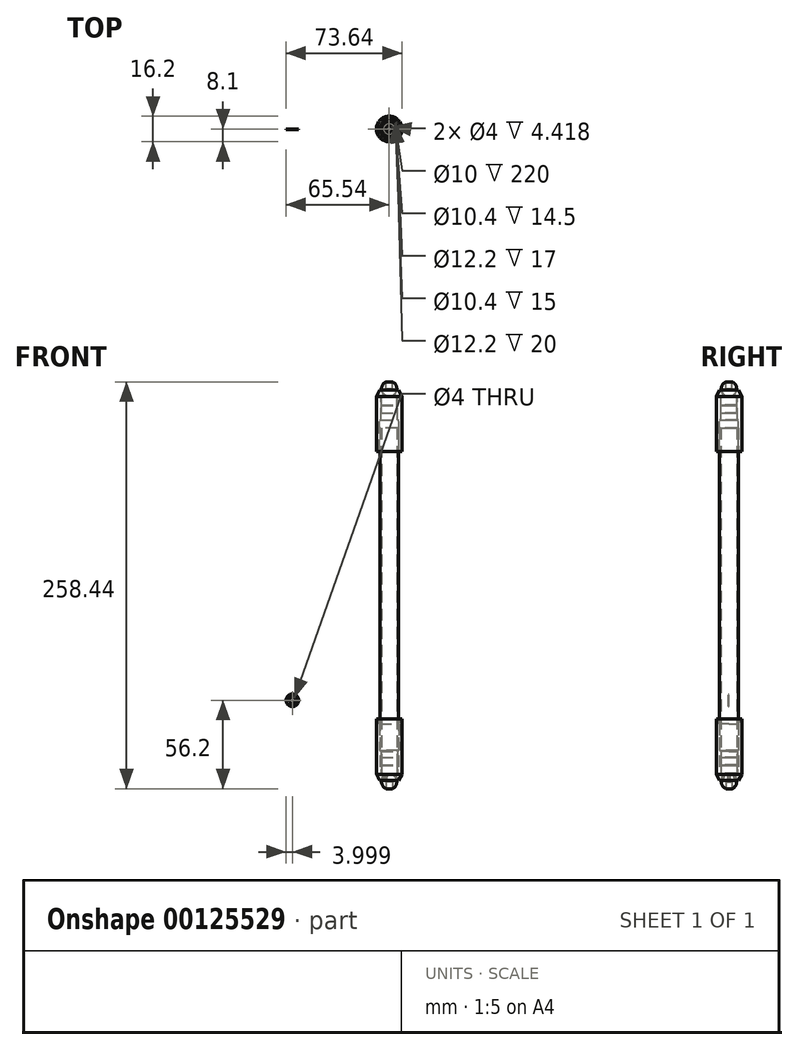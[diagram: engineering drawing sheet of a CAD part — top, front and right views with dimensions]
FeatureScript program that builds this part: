
annotation { "Feature Type Name" : "Feature", "Feature Type Description" : "" }
export const myFeature = defineFeature(function(context is Context, id is Id, definition is map)
    precondition{}
    {
        {
            var Q0;
            Q0=qCreatedBy(makeId("Front.planeOp"),FACE);
            var sketch = newSketch(context, id + "F0", { "sketchPlane" : qUnion([Q0])});
            skLineSegment(sketch, "E0", {"start": v(-5.03, 0.7) * mm, "end": v(-6.03, 0.7) * mm});
            skLineSegment(sketch, "E1", {"start": v(-8.1, 4.8) * mm, "end": v(-8.1, 39.8) * mm});
            skLineSegment(sketch, "E2", {"start": v(-8.1, 39.8) * mm, "end": v(-6.1, 39.8) * mm});
            skLineSegment(sketch, "E3", {"start": v(-6.1, 39.8) * mm, "end": v(-6.1, 19.8) * mm});
            skLineSegment(sketch, "E4", {"start": v(-6.1, 19.8) * mm, "end": v(-5.2, 19.8) * mm});
            skLineSegment(sketch, "E5", {"start": v(-5.2, 19.8) * mm, "end": v(-5.2, 4.8) * mm});
            skLineSegment(sketch, "E6", {"start": v(-5.2, 4.8) * mm, "end": v(-3.11, 4.8) * mm});
            skLineSegment(sketch, "E7", {"start": v(0, 5.2) * mm, "end": v(0, 4.8) * mm});
            skLineSegment(sketch, "E8", {"start": v(-6.03, 0.7) * mm, "end": v(-8.1, 4.8) * mm});
            skLineSegment(sketch, "E9", {"start": v(0, 0) * mm, "end": v(0, 32.36) * mm, "construction": true});
            skLineSegment(sketch, "E10", {"start": v(2.85, 3.2) * mm, "end": v(-9.79, 3.2) * mm, "construction": true});
            skCircle(sketch, "E11", {"center": v(0, 0) * mm, "radius": 4.85 * mm});
            skLineSegment(sketch, "E12", {"start": v(0, 4.8) * mm, "end": v(0, -4.85) * mm});
            skLineSegment(sketch, "E13", {"start": v(0, 15.55) * mm, "end": v(-5, 15.55) * mm});
            skLineSegment(sketch, "E14", {"start": v(-5, 15.55) * mm, "end": v(-5, 10.55) * mm});
            skLineSegment(sketch, "E15", {"start": v(-5, 10.55) * mm, "end": v(0, 10.55) * mm});
            skLineSegment(sketch, "E16", {"start": v(0, 10.55) * mm, "end": v(0, 15.55) * mm});
            skLineSegment(sketch, "E17", {"start": v(0, 5.3) * mm, "end": v(-5, 5.3) * mm});
            skLineSegment(sketch, "E18", {"start": v(-5, 5.3) * mm, "end": v(-5, 10.3) * mm});
            skLineSegment(sketch, "E19", {"start": v(-5, 10.3) * mm, "end": v(0, 10.3) * mm});
            skLineSegment(sketch, "E20", {"start": v(0, 10.3) * mm, "end": v(0, 5.3) * mm});
            skLineSegment(sketch, "E21", {"start": v(-4, 2.74) * mm, "end": v(4, 2.74) * mm, "construction": true});
            skLineSegment(sketch, "E22", {"start": v(0, 11.48) * mm, "end": v(-8.67, -7.13) * mm, "construction": true});
            skLineSegment(sketch, "E23", {"start": v(-5.03, 0.7) * mm, "end": v(-3.11, 4.8) * mm});
            skPoint(sketch, "E24", {"position": v(-4.4, 2.05) * mm});
            skSolve(sketch);
        }
        {
            var Q0;
            Q0=makeQuery(id+"F0.imprint","IMPRINT",FACE,{"disambiguationData":[TD([[makeQuery(id+"F0.imprint","IMPRINT",EDGE,{"derivedFrom":sQuery(id+"F0.wireOp",EDGE,"E13")}),1.0]])]});
            var Q1;
            Q1=makeQuery(id+"F0.imprint","IMPRINT",FACE,{"disambiguationData":[TD([[makeQuery(id+"F0.imprint","IMPRINT",EDGE,{"derivedFrom":sQuery(id+"F0.wireOp",EDGE,"E17")}),-1.0]])]});
            var Q2;
            {var subQ0=sQuery(id+"F0.wireOp",EDGE,"E12");Q2=makeQuery(id+"F0.imprint","IMPRINT",FACE,{"disambiguationData":[TD([[makeQuery(id+"F0.imprint","IMPRINT",EDGE,{"derivedFrom":subQ0}),-1.0]])]});}
            var Q3;
            {var subQ0=sQuery(id+"F0.wireOp",EDGE,"E0");Q3=makeQuery(id+"F0.imprint","IMPRINT",FACE,{"disambiguationData":[TD([[makeQuery(id+"F0.imprint","IMPRINT",EDGE,{"derivedFrom":subQ0}),-1.0]])]});}
            var Q4;
            Q4=sQuery(id+"F0.wireOp",EDGE,"E9");
            revolve(context, id + "F1", {"entities" : qUnion([Q0, Q1, Q2, Q3]), "axis" : qUnion([Q4]), "revolveType" : RevolveType.FULL});
        }
        {
            var Q0;
            Q0=makeQuery(id+"F1.opRevolve","SWEPT_FACE",FACE,{"disambiguationData":[OSD([sQuery(id+"F0.wireOp",EDGE,"E6")])]});
            var sketch = newSketch(context, id + "F2", { "sketchPlane" : qUnion([Q0])});
            skCircle(sketch, "E25", {"center": v(0, 0) * mm, "radius": 6 * mm});
            skCircle(sketch, "E26", {"center": v(0, 0) * mm, "radius": 5 * mm});
            skSolve(sketch);
        }
        {
            var Q0;
            Q0=makeQuery(id+"F2.imprint","IMPRINT",FACE,{"disambiguationData":[TD([[makeQuery(id+"F2.imprint","IMPRINT",EDGE,{"derivedFrom":sQuery(id+"F2.wireOp",EDGE,"E26")}),-1.0]])]});
            var Q1;
            Q1=makeQuery(id+"F2.imprint","IMPRINT",FACE,{"disambiguationData":[TD([[makeQuery(id+"F2.imprint","IMPRINT",EDGE,{"derivedFrom":sQuery(id+"F2.wireOp",EDGE,"E25")}),1.0]])]});
            extrude(context, id + "F3", {"entities" : qUnion([Q0, Q1]), "depth" : 220 * mm});
        }
        {
            var Q0;
            Q0=makeQuery(id+"F3.opExtrude","CAP_FACE",FACE,{"disambiguationData":[OSD([sQuery(id+"F0.wireOp",EDGE,"E4"),sQuery(id+"F0.wireOp",EDGE,"E5"),sQuery(id+"F2.wireOp",EDGE,"E26")])],"isStart":false});
            cPlane(context, id + "F4", {"entities" : qUnion([Q0]), "cplaneType" : CPlaneType.OFFSET, "offset" : 100 * mm, "oppositeDirection" : true, "width" : 150 * mm, "height" : 150 * mm});
        }
        {
            var Q0;
            Q0=qCreatedBy(makeId("Top.planeOp"),FACE);
            cPlane(context, id + "F5", {"entities" : qUnion([Q0]), "cplaneType" : CPlaneType.OFFSET, "offset" : 5 * mm, "oppositeDirection" : true, "width" : 150 * mm, "height" : 150 * mm});
        }
        {
            var Q0;
            Q0=qCreatedBy(id+"F5.planeOp",FACE);
            var sketch = newSketch(context, id + "F6", { "sketchPlane" : qUnion([Q0])});
            skCircle(sketch, "E27", {"center": v(0, 0) * mm, "radius": 2 * mm});
            skSolve(sketch);
        }
        {
            var Q0;
            Q0=makeQuery(id+"F6.imprint","IMPRINT",FACE,{"disambiguationData":[TD([[makeQuery(id+"F6.imprint","IMPRINT",EDGE,{"derivedFrom":sQuery(id+"F6.wireOp",EDGE,"E27")}),1.0]])]});
            extrude(context, id + "F7", {"entities" : qUnion([Q0]), "operationType" : NewBodyOperationType.REMOVE, "depth" : 5 * mm});
        }
        {
            var Q0;
            Q0=makeQuery(id+"F1.opRevolve","SWEPT_BODY",BODY,{"disambiguationData":[OSD([sQuery(id+"F0.wireOp",EDGE,"E17"),sQuery(id+"F0.wireOp",EDGE,"E18"),sQuery(id+"F0.wireOp",EDGE,"E19"),sQuery(id+"F0.wireOp",EDGE,"E20")])]});
            var Q1;
            Q1=makeQuery(id+"F1.opRevolve","SWEPT_BODY",BODY,{"disambiguationData":[OSD([sQuery(id+"F0.wireOp",EDGE,"E13"),sQuery(id+"F0.wireOp",EDGE,"E14"),sQuery(id+"F0.wireOp",EDGE,"E15"),sQuery(id+"F0.wireOp",EDGE,"E16")])]});
            var Q2;
            Q2=makeQuery(id+"F1.opRevolve","SWEPT_BODY",BODY,{"disambiguationData":[OSD([sQuery(id+"F0.wireOp",EDGE,"E11"),sQuery(id+"F0.wireOp",EDGE,"E12")])]});
            var Q3;
            Q3=makeQuery(id+"F1.opRevolve","SWEPT_BODY",BODY,{"disambiguationData":[OSD([sQuery(id+"F0.wireOp",EDGE,"841e1b56-2235-48bc-aee3-342361c37d41"),sQuery(id+"F0.wireOp",EDGE,"E0"),sQuery(id+"F0.wireOp",EDGE,"E1"),sQuery(id+"F0.wireOp",EDGE,"E2"),sQuery(id+"F0.wireOp",EDGE,"E3"),sQuery(id+"F0.wireOp",EDGE,"E4"),sQuery(id+"F0.wireOp",EDGE,"E5"),sQuery(id+"F0.wireOp",EDGE,"E6"),sQuery(id+"F0.wireOp",EDGE,"E8"),sQuery(id+"F0.wireOp",EDGE,"4b548780-3497-4359-ae85-f4aefd225b06")])]});
            var Q4;
            Q4=qCreatedBy(id+"F4.planeOp",FACE);
            mirror(context, id + "F8", {"entities" : qUnion([Q0, Q1, Q2, Q3]), "mirrorPlane" : qUnion([Q4])});
        }
        {
            var Q0;
            Q0=makeQuery(id+"F1.opRevolve","SWEPT_EDGE",EDGE,{"disambiguationData":[OSD([sQuery(id+"F0.wireOp",EDGE,"E2"),sQuery(id+"F0.wireOp",EDGE,"E3")])]});
            var Q1;
            Q1=makeQuery(id+"F1.opRevolve","SWEPT_EDGE",EDGE,{"disambiguationData":[OSD([sQuery(id+"F0.wireOp",EDGE,"E2"),sQuery(id+"F0.wireOp",EDGE,"E3")])]});
            chamfer(context, id + "F9", {"entities" : qUnion([Q0, Q1]), "chamferType" : ChamferType.TWO_OFFSETS, "width1" : 1 * mm, "oppositeDirection" : false, "width2" : 3 * mm, "tangentPropagation" : true});
        }
        {
            var Q0;
            Q0=qCreatedBy(makeId("Front.planeOp"),FACE);
            var sketch = newSketch(context, id + "F10", { "sketchPlane" : qUnion([Q0])});
            skLineSegment(sketch, "E28", {"start": v(-5.5, 0.7) * mm, "end": v(-3.6, 4.8) * mm});
            skLineSegment(sketch, "E29", {"start": v(-5.5, 0.7) * mm, "end": v(-4.14, 0.7) * mm});
            skLineSegment(sketch, "E30", {"start": v(-4.14, 0.7) * mm, "end": v(-2.47, 4.8) * mm});
            skLineSegment(sketch, "E31", {"start": v(-2.47, 4.8) * mm, "end": v(-3.6, 4.8) * mm});
            skLineSegment(sketch, "E32", {"start": v(0, 0) * mm, "end": v(0, -5.1) * mm, "construction": true});
            skSolve(sketch);
        }
        {
            var Q0;
            Q0=makeQuery(id+"F10.imprint","IMPRINT",FACE,{"disambiguationData":[TD([[makeQuery(id+"F10.imprint","IMPRINT",EDGE,{"derivedFrom":sQuery(id+"F10.wireOp",EDGE,"E28")}),-1.0]])]});
            var Q1;
            Q1=sQuery(id+"F10.wireOp",EDGE,"E32");
            revolve(context, id + "F11", {"entities" : qUnion([Q0]), "axis" : qUnion([Q1]), "revolveType" : RevolveType.SYMMETRIC, "angle" : 108 * degree});
        }
        {
            var Q0;
            Q0=makeQuery(id+"F11.opRevolve","SWEPT_BODY",BODY,{"disambiguationData":[OSD([sQuery(id+"F10.wireOp",EDGE,"E28"),sQuery(id+"F10.wireOp",EDGE,"E29"),sQuery(id+"F10.wireOp",EDGE,"E30"),sQuery(id+"F10.wireOp",EDGE,"E31")])]});
            var Q1;
            Q1=sQuery(id+"F10.wireOp",EDGE,"E32");
            circularPattern(context, id + "F12", {"entities" : qUnion([Q0]), "axis" : qUnion([Q1]), "angle" : 120 * degree, "instanceCount" : 3});
        }
        {
            var Q0;
            Q0=makeQuery(id+"F11.opRevolve","SWEPT_BODY",BODY,{"disambiguationData":[OSD([sQuery(id+"F10.wireOp",EDGE,"E28"),sQuery(id+"F10.wireOp",EDGE,"E29"),sQuery(id+"F10.wireOp",EDGE,"E30"),sQuery(id+"F10.wireOp",EDGE,"E31")])]});
            var Q1;
            Q1=makeQuery(id+"F12.opPattern","COPY",BODY,{"derivedFrom":makeQuery(id+"F11.opRevolve","SWEPT_BODY",BODY,{"disambiguationData":[OSD([sQuery(id+"F10.wireOp",EDGE,"E28"),sQuery(id+"F10.wireOp",EDGE,"E29"),sQuery(id+"F10.wireOp",EDGE,"E30"),sQuery(id+"F10.wireOp",EDGE,"E31")])]}),"instanceName":"2"});
            var Q2;
            Q2=makeQuery(id+"F12.opPattern","COPY",BODY,{"derivedFrom":makeQuery(id+"F11.opRevolve","SWEPT_BODY",BODY,{"disambiguationData":[OSD([sQuery(id+"F10.wireOp",EDGE,"E28"),sQuery(id+"F10.wireOp",EDGE,"E29"),sQuery(id+"F10.wireOp",EDGE,"E30"),sQuery(id+"F10.wireOp",EDGE,"E31")])]}),"instanceName":"1"});
            var Q3;
            Q3=makeQuery(id+"F1.opRevolve","SWEPT_BODY",BODY,{"disambiguationData":[OSD([sQuery(id+"F0.wireOp",EDGE,"E0"),sQuery(id+"F0.wireOp",EDGE,"E1"),sQuery(id+"F0.wireOp",EDGE,"E2"),sQuery(id+"F0.wireOp",EDGE,"E3"),sQuery(id+"F0.wireOp",EDGE,"E5"),sQuery(id+"F0.wireOp",EDGE,"E6"),sQuery(id+"F0.wireOp",EDGE,"E8"),sQuery(id+"F0.wireOp",EDGE,"E23")])]});
            booleanBodies(context, id + "F13", {"operationType" : BooleanOperationType.SUBTRACTION, "tools" : qUnion([Q0, Q1, Q2]), "targets" : qUnion([Q3])});
        }
        {
            var Q0;
            Q0=makeQuery(id+"F13.opBoolean","COPY",EDGE,{"derivedFrom":makeQuery(id+"F11.opRevolve","CAP_EDGE",EDGE,{"disambiguationData":[OSD([sQuery(id+"F10.wireOp",EDGE,"E28")])],"isStart":true})});
            var Q1;
            Q1=makeQuery(id+"F13.opBoolean","COPY",EDGE,{"derivedFrom":makeQuery(id+"F12.opPattern","COPY",EDGE,{"derivedFrom":makeQuery(id+"F11.opRevolve","CAP_EDGE",EDGE,{"disambiguationData":[OSD([sQuery(id+"F10.wireOp",EDGE,"E28")])],"isStart":false}),"instanceName":"2"})});
            var Q2;
            Q2=makeQuery(id+"F13.opBoolean","COPY",EDGE,{"derivedFrom":makeQuery(id+"F12.opPattern","COPY",EDGE,{"derivedFrom":makeQuery(id+"F11.opRevolve","CAP_EDGE",EDGE,{"disambiguationData":[OSD([sQuery(id+"F10.wireOp",EDGE,"E28")])],"isStart":true}),"instanceName":"1"})});
            var Q3;
            Q3=makeQuery(id+"F13.opBoolean","COPY",EDGE,{"derivedFrom":makeQuery(id+"F11.opRevolve","CAP_EDGE",EDGE,{"disambiguationData":[OSD([sQuery(id+"F10.wireOp",EDGE,"E28")])],"isStart":false})});
            var Q4;
            Q4=makeQuery(id+"F13.opBoolean","COPY",EDGE,{"derivedFrom":makeQuery(id+"F12.opPattern","COPY",EDGE,{"derivedFrom":makeQuery(id+"F11.opRevolve","CAP_EDGE",EDGE,{"disambiguationData":[OSD([sQuery(id+"F10.wireOp",EDGE,"E28")])],"isStart":true}),"instanceName":"2"})});
            var Q5;
            Q5=makeQuery(id+"F13.opBoolean","COPY",EDGE,{"derivedFrom":makeQuery(id+"F12.opPattern","COPY",EDGE,{"derivedFrom":makeQuery(id+"F11.opRevolve","CAP_EDGE",EDGE,{"disambiguationData":[OSD([sQuery(id+"F10.wireOp",EDGE,"E28")])],"isStart":false}),"instanceName":"1"})});
            fillet(context, id + "F14", {"entities" : qUnion([Q0, Q1, Q2, Q3, Q4, Q5]), "radius" : 0.5 * mm, "tangentPropagation" : true, "allowEdgeOverflow" : false});
        }
        {
            var Q0;
            {var subQ0=sQuery(id+"F10.wireOp",EDGE,"E31");var subQ1=sQuery(id+"F10.wireOp",EDGE,"E30");var subQ2=sQuery(id+"F10.wireOp",EDGE,"E29");var subQ3=sQuery(id+"F10.wireOp",EDGE,"E28");Q0=makeQuery(id+"F14.opFillet","BLEND_EDGE",EDGE,{"blendedFrom":[makeQuery(id+"F13.opBoolean","COPY",EDGE,{"derivedFrom":makeQuery(id+"F11.opRevolve","CAP_EDGE",EDGE,{"disambiguationData":[OSD([subQ3])],"isStart":true})}),makeQuery(id+"F13.opBoolean","SPLIT",FACE,{"disambiguationData":[TD([makeQuery(id+"F11.opRevolve","CAP_FACE",FACE,{"disambiguationData":[OSD([subQ3,subQ2,subQ1,subQ0])],"isStart":true})])],"derivedFrom":makeQuery(id+"F1.opRevolve","SWEPT_FACE",FACE,{"disambiguationData":[OSD([sQuery(id+"F0.wireOp",EDGE,"E23")])]})})],"blendedInto":[makeQuery(id+"F13.opBoolean","SPLIT",FACE,{"disambiguationData":[TD([makeQuery(id+"F11.opRevolve","CAP_FACE",FACE,{"disambiguationData":[OSD([subQ3,subQ2,subQ1,subQ0])],"isStart":true})])],"derivedFrom":makeQuery(id+"F1.opRevolve","SWEPT_FACE",FACE,{"disambiguationData":[OSD([sQuery(id+"F0.wireOp",EDGE,"E23")])]})})]});}
            var Q1;
            {var subQ0=sQuery(id+"F10.wireOp",EDGE,"E31");var subQ1=sQuery(id+"F10.wireOp",EDGE,"E30");var subQ2=sQuery(id+"F10.wireOp",EDGE,"E29");var subQ3=sQuery(id+"F10.wireOp",EDGE,"E28");Q1=makeQuery(id+"F14.opFillet","BLEND_EDGE",EDGE,{"blendedFrom":[makeQuery(id+"F13.opBoolean","COPY",EDGE,{"derivedFrom":makeQuery(id+"F12.opPattern","COPY",EDGE,{"derivedFrom":makeQuery(id+"F11.opRevolve","CAP_EDGE",EDGE,{"disambiguationData":[OSD([subQ3])],"isStart":false}),"instanceName":"2"})}),makeQuery(id+"F13.opBoolean","SPLIT",FACE,{"disambiguationData":[TD([makeQuery(id+"F11.opRevolve","CAP_FACE",FACE,{"disambiguationData":[OSD([subQ3,subQ2,subQ1,subQ0])],"isStart":true})])],"derivedFrom":makeQuery(id+"F1.opRevolve","SWEPT_FACE",FACE,{"disambiguationData":[OSD([sQuery(id+"F0.wireOp",EDGE,"E23")])]})})],"blendedInto":[makeQuery(id+"F13.opBoolean","SPLIT",FACE,{"disambiguationData":[TD([makeQuery(id+"F11.opRevolve","CAP_FACE",FACE,{"disambiguationData":[OSD([subQ3,subQ2,subQ1,subQ0])],"isStart":true})])],"derivedFrom":makeQuery(id+"F1.opRevolve","SWEPT_FACE",FACE,{"disambiguationData":[OSD([sQuery(id+"F0.wireOp",EDGE,"E23")])]})})]});}
            var Q2;
            {var subQ0=sQuery(id+"F10.wireOp",EDGE,"E31");var subQ1=sQuery(id+"F10.wireOp",EDGE,"E30");var subQ2=sQuery(id+"F10.wireOp",EDGE,"E29");var subQ3=sQuery(id+"F10.wireOp",EDGE,"E28");Q2=makeQuery(id+"F14.opFillet","BLEND_EDGE",EDGE,{"blendedFrom":[makeQuery(id+"F13.opBoolean","COPY",EDGE,{"derivedFrom":makeQuery(id+"F12.opPattern","COPY",EDGE,{"derivedFrom":makeQuery(id+"F11.opRevolve","CAP_EDGE",EDGE,{"disambiguationData":[OSD([subQ3])],"isStart":true}),"instanceName":"1"})}),makeQuery(id+"F13.opBoolean","SPLIT",FACE,{"disambiguationData":[TD([makeQuery(id+"F11.opRevolve","CAP_FACE",FACE,{"disambiguationData":[OSD([subQ3,subQ2,subQ1,subQ0])],"isStart":false})])],"derivedFrom":makeQuery(id+"F1.opRevolve","SWEPT_FACE",FACE,{"disambiguationData":[OSD([sQuery(id+"F0.wireOp",EDGE,"E23")])]})})],"blendedInto":[makeQuery(id+"F13.opBoolean","SPLIT",FACE,{"disambiguationData":[TD([makeQuery(id+"F11.opRevolve","CAP_FACE",FACE,{"disambiguationData":[OSD([subQ3,subQ2,subQ1,subQ0])],"isStart":false})])],"derivedFrom":makeQuery(id+"F1.opRevolve","SWEPT_FACE",FACE,{"disambiguationData":[OSD([sQuery(id+"F0.wireOp",EDGE,"E23")])]})})]});}
            var Q3;
            {var subQ0=sQuery(id+"F10.wireOp",EDGE,"E31");var subQ1=sQuery(id+"F10.wireOp",EDGE,"E30");var subQ2=sQuery(id+"F10.wireOp",EDGE,"E29");var subQ3=sQuery(id+"F10.wireOp",EDGE,"E28");Q3=makeQuery(id+"F14.opFillet","BLEND_EDGE",EDGE,{"blendedFrom":[makeQuery(id+"F13.opBoolean","COPY",EDGE,{"derivedFrom":makeQuery(id+"F11.opRevolve","CAP_EDGE",EDGE,{"disambiguationData":[OSD([subQ3])],"isStart":false})}),makeQuery(id+"F13.opBoolean","SPLIT",FACE,{"disambiguationData":[TD([makeQuery(id+"F11.opRevolve","CAP_FACE",FACE,{"disambiguationData":[OSD([subQ3,subQ2,subQ1,subQ0])],"isStart":false})])],"derivedFrom":makeQuery(id+"F1.opRevolve","SWEPT_FACE",FACE,{"disambiguationData":[OSD([sQuery(id+"F0.wireOp",EDGE,"E23")])]})})],"blendedInto":[makeQuery(id+"F13.opBoolean","SPLIT",FACE,{"disambiguationData":[TD([makeQuery(id+"F11.opRevolve","CAP_FACE",FACE,{"disambiguationData":[OSD([subQ3,subQ2,subQ1,subQ0])],"isStart":false})])],"derivedFrom":makeQuery(id+"F1.opRevolve","SWEPT_FACE",FACE,{"disambiguationData":[OSD([sQuery(id+"F0.wireOp",EDGE,"E23")])]})})]});}
            var Q4;
            {var subQ0=sQuery(id+"F10.wireOp",EDGE,"E31");var subQ1=sQuery(id+"F10.wireOp",EDGE,"E30");var subQ2=sQuery(id+"F10.wireOp",EDGE,"E29");var subQ3=sQuery(id+"F10.wireOp",EDGE,"E28");Q4=makeQuery(id+"F14.opFillet","BLEND_EDGE",EDGE,{"blendedFrom":[makeQuery(id+"F13.opBoolean","COPY",EDGE,{"derivedFrom":makeQuery(id+"F12.opPattern","COPY",EDGE,{"derivedFrom":makeQuery(id+"F11.opRevolve","CAP_EDGE",EDGE,{"disambiguationData":[OSD([subQ3])],"isStart":false}),"instanceName":"1"})}),makeQuery(id+"F13.opBoolean","SPLIT",FACE,{"disambiguationData":[TD([makeQuery(id+"F12.opPattern","COPY",FACE,{"derivedFrom":makeQuery(id+"F11.opRevolve","CAP_FACE",FACE,{"disambiguationData":[OSD([subQ3,subQ2,subQ1,subQ0])],"isStart":false}),"instanceName":"1"})])],"derivedFrom":makeQuery(id+"F1.opRevolve","SWEPT_FACE",FACE,{"disambiguationData":[OSD([sQuery(id+"F0.wireOp",EDGE,"E23")])]})})],"blendedInto":[makeQuery(id+"F13.opBoolean","SPLIT",FACE,{"disambiguationData":[TD([makeQuery(id+"F12.opPattern","COPY",FACE,{"derivedFrom":makeQuery(id+"F11.opRevolve","CAP_FACE",FACE,{"disambiguationData":[OSD([subQ3,subQ2,subQ1,subQ0])],"isStart":false}),"instanceName":"1"})])],"derivedFrom":makeQuery(id+"F1.opRevolve","SWEPT_FACE",FACE,{"disambiguationData":[OSD([sQuery(id+"F0.wireOp",EDGE,"E23")])]})})]});}
            var Q5;
            {var subQ0=sQuery(id+"F10.wireOp",EDGE,"E31");var subQ1=sQuery(id+"F10.wireOp",EDGE,"E30");var subQ2=sQuery(id+"F10.wireOp",EDGE,"E29");var subQ3=sQuery(id+"F10.wireOp",EDGE,"E28");Q5=makeQuery(id+"F14.opFillet","BLEND_EDGE",EDGE,{"blendedFrom":[makeQuery(id+"F13.opBoolean","COPY",EDGE,{"derivedFrom":makeQuery(id+"F12.opPattern","COPY",EDGE,{"derivedFrom":makeQuery(id+"F11.opRevolve","CAP_EDGE",EDGE,{"disambiguationData":[OSD([subQ3])],"isStart":true}),"instanceName":"2"})}),makeQuery(id+"F13.opBoolean","SPLIT",FACE,{"disambiguationData":[TD([makeQuery(id+"F12.opPattern","COPY",FACE,{"derivedFrom":makeQuery(id+"F11.opRevolve","CAP_FACE",FACE,{"disambiguationData":[OSD([subQ3,subQ2,subQ1,subQ0])],"isStart":false}),"instanceName":"1"})])],"derivedFrom":makeQuery(id+"F1.opRevolve","SWEPT_FACE",FACE,{"disambiguationData":[OSD([sQuery(id+"F0.wireOp",EDGE,"E23")])]})})],"blendedInto":[makeQuery(id+"F13.opBoolean","SPLIT",FACE,{"disambiguationData":[TD([makeQuery(id+"F12.opPattern","COPY",FACE,{"derivedFrom":makeQuery(id+"F11.opRevolve","CAP_FACE",FACE,{"disambiguationData":[OSD([subQ3,subQ2,subQ1,subQ0])],"isStart":false}),"instanceName":"1"})])],"derivedFrom":makeQuery(id+"F1.opRevolve","SWEPT_FACE",FACE,{"disambiguationData":[OSD([sQuery(id+"F0.wireOp",EDGE,"E23")])]})})]});}
            fillet(context, id + "F15", {"entities" : qUnion([Q0, Q1, Q2, Q3, Q4, Q5]), "radius" : 0.5 * mm, "tangentPropagation" : true, "allowEdgeOverflow" : false});
        }
        {
            var Q0;
            Q0=makeQuery(id+"F1.opRevolve","SWEPT_EDGE",EDGE,{"disambiguationData":[OSD([sQuery(id+"F0.wireOp",EDGE,"E4"),sQuery(id+"F0.wireOp",EDGE,"E5")])]});
            chamfer(context, id + "F16", {"entities" : qUnion([Q0]), "width" : 0.5 * mm, "tangentPropagation" : true});
        }
        {
            var Q0;
            Q0=qCreatedBy(makeId("Front.planeOp"),FACE);
            var sketch = newSketch(context, id + "F17", { "sketchPlane" : qUnion([Q0])});
            skCircle(sketch, "E33", {"center": v(-61.54, 51.78) * mm, "radius": 2 * mm});
            skCircle(sketch, "E34", {"center": v(-61.54, 51.78) * mm, "radius": 4 * mm});
            skSolve(sketch);
        }
        {
            var Q0;
            Q0=makeQuery(id+"F17.imprint","IMPRINT",FACE,{"disambiguationData":[TD([[makeQuery(id+"F17.imprint","IMPRINT",EDGE,{"derivedFrom":sQuery(id+"F17.wireOp",EDGE,"E33")}),-1.0]])]});
            extrude(context, id + "F18", {"entities" : qUnion([Q0]), "depth" : 0.5 * mm});
        }
    });
